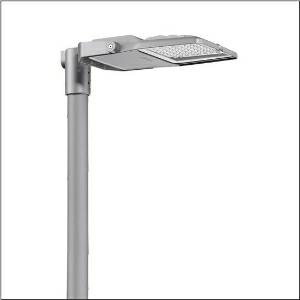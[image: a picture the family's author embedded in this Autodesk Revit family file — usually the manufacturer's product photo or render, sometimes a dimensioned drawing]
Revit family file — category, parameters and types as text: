
# Revit family: floodlight_fl_21_mini___pl33t_5xa7776b2f3a_1e67
name_source: partatom
category: Lighting Fixtures
units: mm (PartAtom-declared; Revit-internal decimal feet)

## family parameters
Cut with Voids When Loaded = No
Host = Face
Light Source = No
Part Type = Normal
Room Calculation Point = No
Round Connector Dimension = Use Diameter
Shared = No

## types (1)
- --- (1 x LED, 6150 lm, 45.7 W, 3000K)
    Apparent Load = 46 VA
    CIE Flux Codes = 26 75 99 100 100
    Color Rendering = 70
    Color Temperature = 3000K
    Default Elevation = 1800 mm
    Description = Floodlight FL 21 mini, floodlight, primary light control with lens, of PMMA, primary optical cover: protective disc, of toughened safety glass, transparent, light distribution: PL33T, light emission: direct distribution, installation type: surface-mounted, LED, High Power LED, rated luminous flux: 6.150lm, luminous efficacy: 135lm/W, light colour: 730, colour temperature: 3000K, control gear: Smart Interface (Zhaga), control: flexible luminous flux parameterisation, time-dependent luminous flux control, constant luminous flux control, overheat protection, pre-setting: logarithmic dimming characteristic, with terminal, 6-pole, mains connection: 220..240V, AC, 50/60Hz, start of lifetime: 46W, end of service life: 48W, reduction: 22W, luminaire housing, of diecast aluminium, powder-coated, Siteco® metallic grey (DB 702S), corrosivity category C5 mid according to DIN EN ISO 12944, suitable for swimming pools, chlorine-resistant, sealing non-destructively replaceable, please order mast flange separately, mast bracket, of steel, galvanised, powder-coated, Siteco® metallic grey (DB 702S), Smart Interface below and above, protection rating (complete): IP66, insulation class (complete): insulation class II (safety insulation), certification: CE, ENEC, VDE, protection symbol: D, impact resistance: IK08, permissible operating ambient temperature: -40..+40°C, permissible operating ambient temperature for outdoor applications: -40..+50°C, standard: DIN EN 12944, LABS conformity tested according to VDMA 24364:2018-05, packaging unit: 1 piece

Light Distribution: PL33T
    Height = 70 mm
    Lamp = 1 x LED
    Lamp Light Flux = 6150 lm
    Lamp Power = 45.7 W
    Lamp count = 1
    Length = 485 mm
    Luminous efficacy = 135 lm/W
    Manufacturer = Siteco
    ModVariant = No
    Model = 5XA7776B2F3A
    Number of Poles = 1
    OnlyDefault = Yes
    Power Factor = 1
    Product Name = Floodlight FL 21 mini | PL33T
    Product group = floodlight | pylon annexe
    ProductGroupID = 6200
    Protection Class = Protection class II
    Protection Degree = IP 66
    RLX_Detail_Level = 1
    RLX_Emergency_Light_Flux = 0 lm
    RLX_Emergency_Type = 0
    RLX_Emergency_Type_DB = No
    RlxData = <blob elided: 101009 chars, md5=72ba5d94>
    Socket = socket
    Standby Power = 0 W
    System Light Flux = 6150 lm
    System Power = 46 W
    Type Comments = factory setting: luminous flux: 100 % | dim-lin: 254 | 463 mA
    Type Image = l_1007125.jpg
    URL = http://relux.com
    VarID = @adj_148606
    Voltage = 0 V
    Weight = 0.00 kg
    Width = 337 mm

## geometry (parser evidence)
native form markers: Blend x4, Sweep x11
no freeform markers — native parametric forms only
